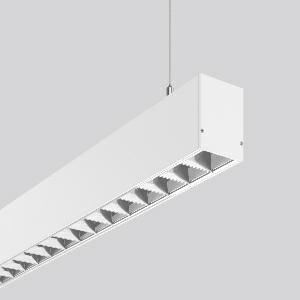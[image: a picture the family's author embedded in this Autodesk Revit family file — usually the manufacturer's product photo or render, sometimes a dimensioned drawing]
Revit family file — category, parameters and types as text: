
# Revit family: less_is_more_50_312341_002_76_e695
name_source: partatom
category: Lighting Fixtures
units: mm (PartAtom-declared; Revit-internal decimal feet)

## family parameters
Cut with Voids When Loaded = No
Host = Face
Light Source = No
Part Type = Normal
Room Calculation Point = No
Round Connector Dimension = Use Diameter
Shared = No

## types (1)
- LESS IS MORE 50 (1 x LED Modul 830, 3950 lm, 3000)
    Apparent Load = 35 VA
    CIE Flux Codes = 95 100 100 63 100
    Color Rendering = 80
    Color Temperature = 3000
    Default Elevation = 1800 mm
    Description = Series: LESS IS MORE 50
Linear pendant luminaire for aesthetically sophisticated lighting. Housing: extruded aluminium profile, powder-coated. End cap aluminium powder-coated. Canopy made of aluminium, powder-coated. Alea optical system: Reflector structure (ABS, Aluminium-coated, highly polished) with integrated diffuser made of non-yellowing plastic (PMMA) opal for glare-free light at the workstation (screen-compliant according to EN 12464-1). Direct 65%, indirect 35% light emission. Controlled separately. Suitable for pendant. 2-point steel cable suspension freely positionable and infinitely height-adjustable. Special lengths available on request. LED unit with integrated converter interchangeable and removable. Suitable for through-wiring. With sensors or as a safety luminaire on request. 
Colour: traffic white, matt (RAL 9016)
Length: 847 mm
Width: 57 mm
Height: 75 mm
Suspension length: 2000 mm
Lamp: LED
Socket: without socket
Colour temperature: 3000K
Colour rendering index (CRI): 80
Light source: LED
Socket lamp2: Without base
Colour temperature: 3000K
System power: 35 W
Rated luminous flux: 3950 lm
Luminous efficiency: 113 lm/W
Control gear: Converter, dimmable, DALI
Control gear: Converter, dimmable, DALI
Protection class: I
Type of protection: IP 20
    Height = 75 mm
    Lamp = 1 x LED Modul 830
    Lamp Light Flux = 3950 lm
    Lamp count = 1
    Length = 847 mm
    Lifetime = 50000 h
    Luminous efficacy = 113 lm/W
    Manufacturer = RZB
    ModVariant = No
    Model = 312341.002.76
    Mounting Place = Ceiling
    Mounting Type = Pendant
    Number of Poles = 1
    OnlyDefault = Yes
    Power Factor = 1
    Product Name = LESS IS MORE 50
    Product group = Pendant LED linear luminaires
    ProductGroupID = 907
    Protection Class = Protection class I
    Protection Degree = IP 20
    RLX_Detail_Level = 1
    RLX_Emergency_Light_Flux = 0 lm
    RLX_Emergency_Type = 0
    RLX_Emergency_Type_DB = No
    RlxData = <blob elided: 37401 chars, md5=b553e096>
    Socket = socket
    Standby Power = 0 W
    System Light Flux = 3950 lm
    System Power = 35 W
    Type Comments = Product without accessories
    Type Image = 312342.002.jpg
    URL = http://relux.com
    VarID = ---
    Voltage = 230 V
    Voltage Range = 220-240 V
    Weight = 0.00 kg
    Width = 57 mm

## geometry (parser evidence)
native form markers: Blend x4, Sweep x14
no freeform markers — native parametric forms only
